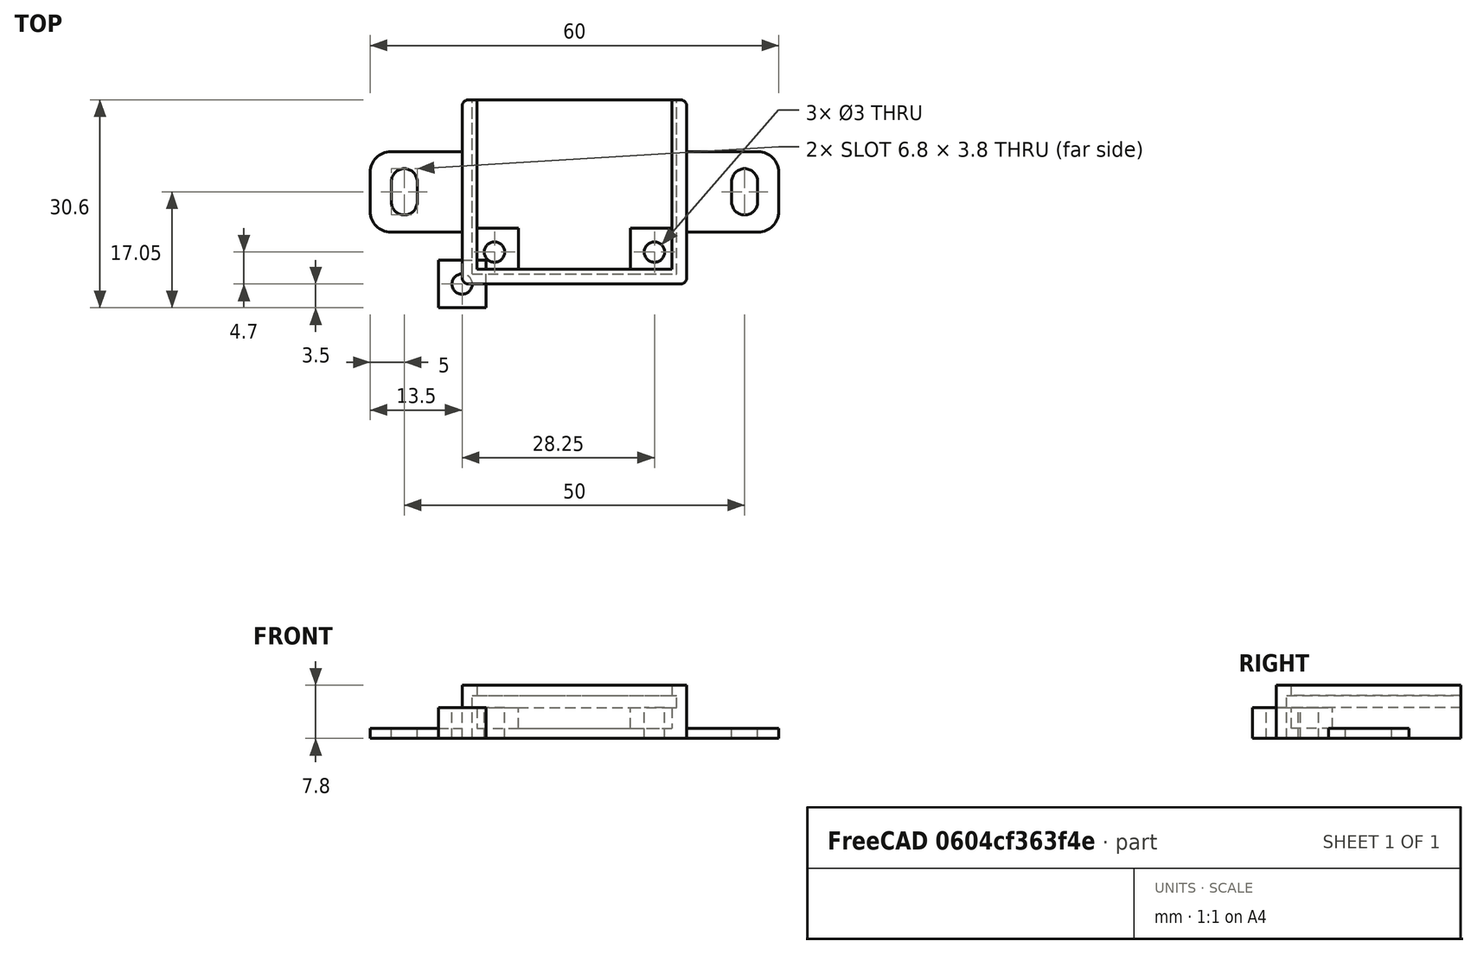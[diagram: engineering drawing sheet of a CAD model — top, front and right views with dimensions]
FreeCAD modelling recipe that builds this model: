
FCSTD DOCUMENT  (FreeCAD 0.19R23578 (Git))
Label: zs-x9b_bldc_motor_driver
License: FreeArt
LicenseURL: http://artlibre.org/licence/lal
objects: Part::Box×4, Part::MultiFuse×3, Part::Cut×3, Part::FeaturePython×2, Spreadsheet::Sheet×1, Part::Fillet×1, Part::Cylinder×1, Part::Feature×1, App::Part×1
note: 13 computed .brp shape members not serialized (recipe doc carries the construction recipe); baked Part::Feature solids carry a one-line shape summary decoded from their .brp

FEATURE [Spreadsheet::Sheet] Spreadsheet  label="p"
  cells = A1=pcb_x; B1(pcb_x)=30; A2=pcb_y; B2(pcb_y)=25.6; A3=pcb_z; B3(pcb_z)=1.8; A4=pcb_under; B4(pcb_under)=3; A5=side_wall; B5(side_wall)=1.5; A6=pcb_side_lane; B6(pcb_side_lane)=0.7; A7=bottom_wall; B7(bottom_wall)=1.5; A8=pcb_above; B8(pcb_above)=1.5; A9=hole_dist_x; B9(hole_dist_x)=23.5; A10=hole_r; B10(hole_r)=1.5; A11=hole_off_y; B11(hole_off_y)=3.2; A12=hole_stand_size; B12(hole_stand_size)=7
FEATURE [Part::Box] Box  label="external cube"
  AttacherType = Attacher::AttachEngine3D
  Height = 7.8
  Length = 33
  Width = 27.1
  expr: Length = <<p>>.pcb_x + 2 * <<p>>.side_wall
  expr: Width = <<p>>.pcb_y + <<p>>.side_wall
  expr: Height = <<p>>.bottom_wall + <<p>>.pcb_under + <<p>>.pcb_z + <<p>>.pcb_above
FEATURE [Part::Box] Box006  label="internal cube"
  AttacherType = Attacher::AttachEngine3D
  Height = 6.3
  Length = 28.6
  Placement = pos=(2.2,2.2,1.5) rot=(0,0,1;0rad)
  Width = 25.7
  expr: Length = <<p>>.pcb_x - 2 * <<p>>.pcb_side_lane
  expr: Width = <<p>>.pcb_y - 2 * <<p>>.pcb_side_lane + <<p>>.side_wall
  expr: Height = <<p>>.pcb_under + <<p>>.pcb_z + <<p>>.pcb_above
  expr: .Placement.Base.z = <<p>>.bottom_wall
  expr: .Placement.Base.x = <<p>>.side_wall + <<p>>.pcb_side_lane
  expr: .Placement.Base.y = <<p>>.side_wall + <<p>>.pcb_side_lane
FEATURE [Part::Box] Box007  label="pcb extract cube"
  AttacherType = Attacher::AttachEngine3D
  Height = 1.8
  Length = 30
  Placement = pos=(1.5,1.5,4.5) rot=(0,0,1;0rad)
  Width = 25.6
  expr: Height = <<p>>.pcb_z
  expr: .Placement.Base.z = <<p>>.bottom_wall + <<p>>.pcb_under
  expr: Width = <<p>>.pcb_y
  expr: Length = <<p>>.pcb_x
  expr: .Placement.Base.x = <<p>>.side_wall
  expr: .Placement.Base.y = <<p>>.side_wall
FEATURE [Part::MultiFuse] Fusion  label="extract fusion"
  Shapes = -> [Box006,Box007]
FEATURE [Part::Fillet] Fillet  label="external fillet"
  Base = -> Box
  Edges = 4 edges r=1: [Edge1,Edge3,Edge5,Edge7]
FEATURE [Part::Cylinder] Cylinder  label="hole"
  Angle = 360
  AttacherType = Attacher::AttachEngine3D
  Height = 10
  Radius = 1.5
  expr: Radius = <<p>>.hole_r
FEATURE [Part::Box] Box008  label="stand"
  AttacherType = Attacher::AttachEngine3D
  Height = 4.5
  Length = 7
  Placement = pos=(-3.5,-3.5,0) rot=(0,0,1;0rad)
  Width = 7
  expr: .Placement.Base.y = -<<p>>.hole_stand_size / 2
  expr: .Placement.Base.x = -<<p>>.hole_stand_size / 2
  expr: Width = <<p>>.hole_stand_size
  expr: Length = <<p>>.hole_stand_size
  expr: Height = <<p>>.pcb_under + <<p>>.bottom_wall
FEATURE [Part::FeaturePython] Array  label="hole array"  # Draft array (typed FeaturePython)
  Angle = 360
  ArrayType = 0
  Axis = (0,0,1)
  Base = -> Box008
  Center = (0,0,0)
  Count = 2
  ExpandArray = false
  Fuse = false
  IntervalAxis = (0,0,0)
  IntervalX = (23.5,0,0)
  IntervalY = (0,1,0)
  IntervalZ = (0,0,100)
  NumberCircles = 3
  NumberPolar = 5
  NumberX = 2
  NumberY = 1
  NumberZ = 1
  Placement = pos=(4.75,4.7,0) rot=(0,0,1;0rad)
  PlacementList = 2 placements: [(-3.5,-3.5,0),(20,-3.5,0)]
  RadialDistance = 50
  ScaleList = (2) [(1,1,1),(1,1,1)]
  Symmetry = 1
  TangentialDistance = 25
  expr: .IntervalX.x = Spreadsheet.hole_dist_x
  expr: .Placement.Base.x = (2 * <<p>>.side_wall + <<p>>.pcb_x - Spreadsheet.hole_dist_x) / 2
  expr: .Placement.Base.y = Spreadsheet.hole_off_y + <<p>>.side_wall
FEATURE [Part::Cut] Cut003002  label="stand hole cut"
  Base = -> Box008
  Tool = -> Cylinder
FEATURE [Part::FeaturePython] Array001  label="hole array001"  # Draft array (typed FeaturePython)
  Angle = 360
  ArrayType = 0
  Axis = (0,0,1)
  Base = -> Cylinder
  Center = (0,0,0)
  Count = 2
  ExpandArray = false
  Fuse = false
  IntervalAxis = (0,0,0)
  IntervalX = (23.5,0,0)
  IntervalY = (0,1,0)
  IntervalZ = (0,0,100)
  NumberCircles = 3
  NumberPolar = 5
  NumberX = 2
  NumberY = 1
  NumberZ = 1
  Placement = pos=(4.75,4.7,0) rot=(0,0,1;0rad)
  PlacementList = 2 placements: [(0,0,0),(23.5,0,0)]
  RadialDistance = 50
  ScaleList = (2) [(1,1,1),(1,1,1)]
  Symmetry = 1
  TangentialDistance = 25
  expr: .Placement.Base.y = Spreadsheet.hole_off_y + <<p>>.side_wall
  expr: .Placement.Base.x = (2 * <<p>>.side_wall + <<p>>.pcb_x - Spreadsheet.hole_dist_x) / 2
  expr: .IntervalX.x = Spreadsheet.hole_dist_x
FEATURE [Part::Feature] Cut003004  label="attach plane x dir002"
  Placement = pos=(-13.5,7.65,0) rot=(0,0,1;0rad)
  shape: bbox 60 x 11.8 x 1.5 mm, 18 faces (baked)
FEATURE [Part::MultiFuse] Fusion001  label="body fusion"
  Shapes = -> [Fillet,Cut003004]
FEATURE [Part::Cut] Cut  label="body cut003"
  Base = -> Fusion001
  Tool = -> Fusion
FEATURE [Part::MultiFuse] Fusion002  label="body fusion003"
  Shapes = -> [Array,Cut]
FEATURE [Part::Cut] Cut003003  label="body cut"
  Base = -> Fusion002
  Tool = -> Array001
FEATURE [App::Part] Part  label="box part"
  Group = -> [Box,Fillet,Fusion001,Fusion,Box007,Box006,Cut,Cylinder,Box008,Cut003002,Array,Fusion002,Array001,Cut003003]
  Origin = -> Origin
